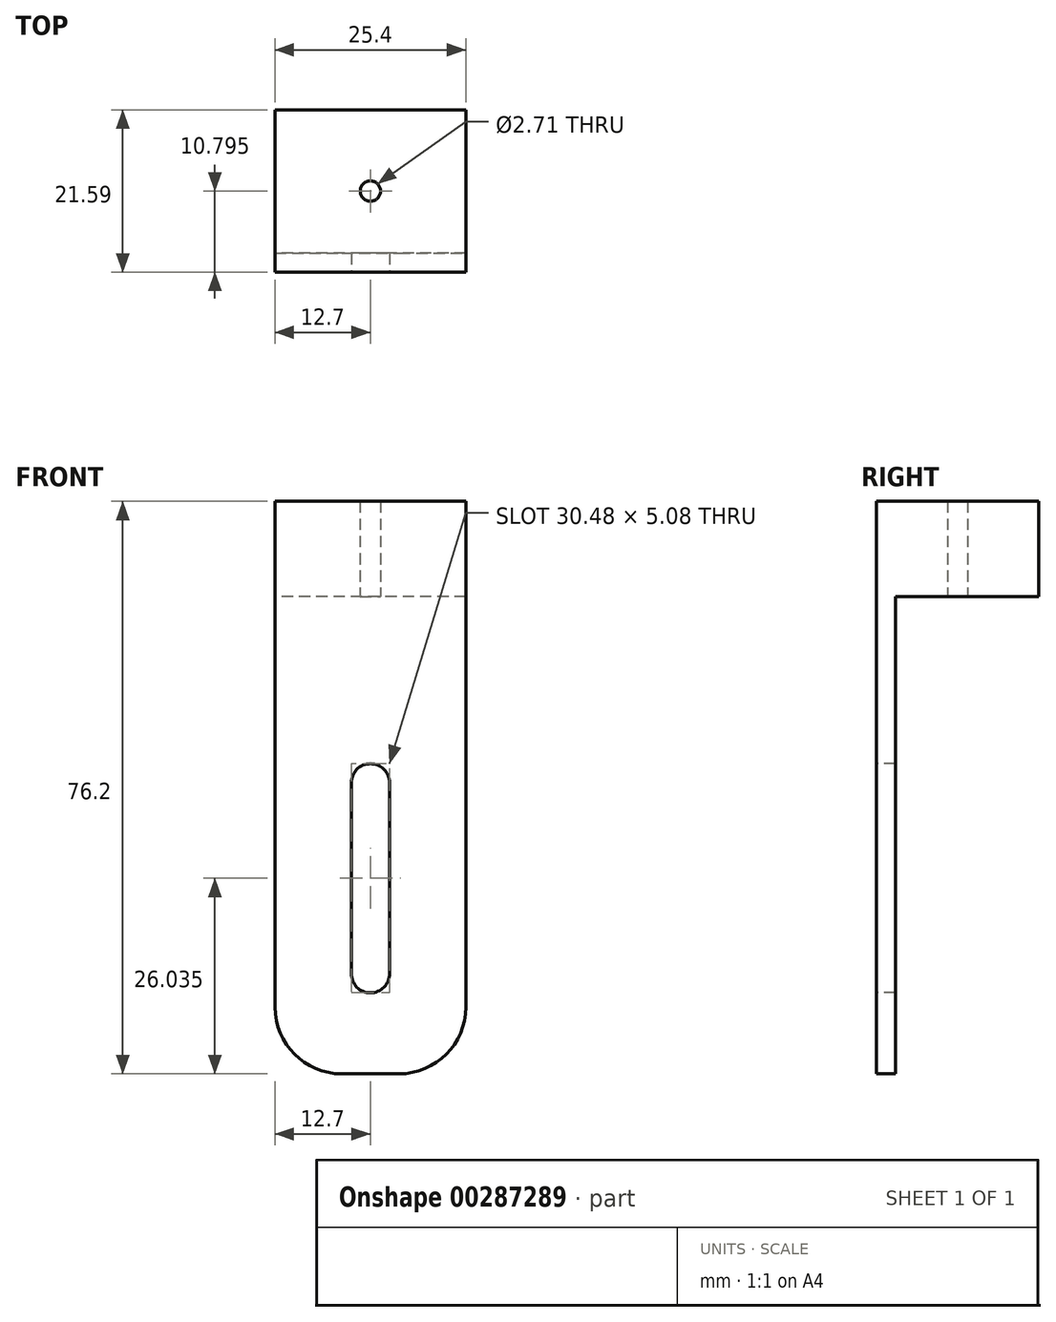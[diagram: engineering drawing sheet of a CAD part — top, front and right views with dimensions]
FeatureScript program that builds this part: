
annotation { "Feature Type Name" : "Feature", "Feature Type Description" : "" }
export const myFeature = defineFeature(function(context is Context, id is Id, definition is map)
    precondition{}
    {
        {
            var Q0;
            Q0=qCreatedBy(makeId("Front.planeOp"),FACE);
            var sketch = newSketch(context, id + "F0", { "sketchPlane" : qUnion([Q0])});
            skLineSegment(sketch, "E0.bottom", {"start": v(0, 0) * mm, "end": v(25.4, 0) * mm});
            skLineSegment(sketch, "E0.top", {"start": v(0, 76.2) * mm, "end": v(25.4, 76.2) * mm});
            skLineSegment(sketch, "E0.left", {"start": v(0, 0) * mm, "end": v(0, 76.2) * mm});
            skLineSegment(sketch, "E0.right", {"start": v(25.4, 0) * mm, "end": v(25.4, 76.2) * mm});
            skSolve(sketch);
        }
        {
            var Q0;
            Q0=qSketchRegion(id+"F0",true);
            extrude(context, id + "F1", {"entities" : qUnion([Q0]), "depth" : 2.54 * mm, "offsetDistance" : 25.4 * mm});
        }
        {
            var Q0;
            Q0=makeQuery(id+"F1.opExtrude","CAP_FACE",FACE,{"disambiguationData":[OSD([sQuery(id+"F0.wireOp",EDGE,"E0.bottom"),sQuery(id+"F0.wireOp",EDGE,"E0.top"),sQuery(id+"F0.wireOp",EDGE,"E0.left"),sQuery(id+"F0.wireOp",EDGE,"E0.right")])],"isStart":true});
            var sketch = newSketch(context, id + "F2", { "sketchPlane" : qUnion([Q0])});
            skLineSegment(sketch, "E1.bottom", {"start": v(-25.4, 76.2) * mm, "end": v(0, 76.2) * mm});
            skLineSegment(sketch, "E1.top", {"start": v(-25.4, 63.5) * mm, "end": v(0, 63.5) * mm});
            skLineSegment(sketch, "E1.left", {"start": v(-25.4, 76.2) * mm, "end": v(-25.4, 63.5) * mm});
            skLineSegment(sketch, "E1.right", {"start": v(0, 76.2) * mm, "end": v(0, 63.5) * mm});
            skSolve(sketch);
        }
        {
            var Q0;
            Q0=qSketchRegion(id+"F2",true);
            extrude(context, id + "F3", {"entities" : qUnion([Q0]), "operationType" : NewBodyOperationType.ADD, "depth" : 19.05 * mm, "offsetDistance" : 25.4 * mm});
        }
        {
            var Q0;
            Q0=makeQuery(id+"F3.opExtrude","SWEPT_FACE",FACE,{"disambiguationData":[OSD([sQuery(id+"F2.wireOp",EDGE,"E1.top")])]});
            var sketch = newSketch(context, id + "F4", { "sketchPlane" : qUnion([Q0])});
            skPoint(sketch, "E2", {"position": v(12.7, -8.26) * mm});
            skLineSegment(sketch, "E3", {"start": v(12.7, -19.05) * mm, "end": v(12.7, 0) * mm, "construction": true});
            skSolve(sketch);
        }
        {
            var Q0;
            Q0=sQuery(id+"F4.wireOp",VERTEX,"E2");
            var Q1;
            Q1=makeQuery(id+"F1.opExtrude","SWEPT_BODY",BODY,{"disambiguationData":[OSD([sQuery(id+"F0.wireOp",EDGE,"E0.bottom"),sQuery(id+"F0.wireOp",EDGE,"E0.top"),sQuery(id+"F0.wireOp",EDGE,"E0.left"),sQuery(id+"F0.wireOp",EDGE,"E0.right")])]});
            hole(context, id + "F5", {"style" : HoleStyle.SIMPLE, "endStyle" : HoleEndStyle.THROUGH, "standardTappedOrClearance" : lookupTablePath({ "standard" : "ANSI", "engagement" : "75%", "pitch" : "32 tpi", "size" : "#6", "type" : "Tapped" }), "standardBlindInLast" : lookupTablePath({ "standard" : "ANSI", "engagement" : "75%", "pitch" : "32 tpi", "size" : "#6", "type" : "Tapped" }), "holeDiameter" : 2.7 * mm, "majorDiameter" : 3.5 * mm, "showTappedDepth" : true, "isTappedThrough" : true, "tappedDepth" : 10.32 * mm, "tapClearance" : 3, "startFromSketch" : true, "locations" : qUnion([Q0]), "scope" : qUnion([Q1])});
        }
        {
            var Q0;
            Q0=makeQuery(id+"F1.opExtrude","CAP_FACE",FACE,{"disambiguationData":[OSD([sQuery(id+"F0.wireOp",EDGE,"E0.bottom"),sQuery(id+"F0.wireOp",EDGE,"E0.top"),sQuery(id+"F0.wireOp",EDGE,"E0.left"),sQuery(id+"F0.wireOp",EDGE,"E0.right")])],"isStart":false});
            var sketch = newSketch(context, id + "F6", { "sketchPlane" : qUnion([Q0])});
            skLineSegment(sketch, "E4", {"start": v(12.7, 38.74) * mm, "end": v(12.7, 13.34) * mm});
            skArc(sketch, "E5.0.startCap", {"start": v(10.16, 38.74) * mm, "mid": v(12.7, 41.28) * mm, "end": v(15.24, 38.74) * mm});
            skArc(sketch, "E5.0.endCap", {"start": v(15.24, 13.34) * mm, "mid": v(12.7, 10.8) * mm, "end": v(10.16, 13.34) * mm});
            skLineSegment(sketch, "E5.0.left", {"start": v(15.24, 38.74) * mm, "end": v(15.24, 13.33) * mm});
            skLineSegment(sketch, "E5.0.right", {"start": v(10.16, 38.74) * mm, "end": v(10.16, 13.34) * mm});
            skLineSegment(sketch, "E6", {"start": v(12.7, 0) * mm, "end": v(12.7, 76.2) * mm, "construction": true});
            skSolve(sketch);
        }
        {
            var Q0;
            Q0=qSketchRegion(id+"F6",true);
            extrude(context, id + "F7", {"entities" : qUnion([Q0]), "operationType" : NewBodyOperationType.REMOVE, "endBound" : BoundingType.THROUGH_ALL, "oppositeDirection" : true, "depth" : 25.4 * mm, "offsetDistance" : 25.4 * mm});
        }
        {
            var Q0;
            Q0=makeQuery(id+"F1.opExtrude","SWEPT_EDGE",EDGE,{"disambiguationData":[OSD([sQuery(id+"F0.wireOp",EDGE,"E0.bottom"),sQuery(id+"F0.wireOp",EDGE,"E0.left")])]});
            var Q1;
            Q1=makeQuery(id+"F1.opExtrude","SWEPT_EDGE",EDGE,{"disambiguationData":[OSD([sQuery(id+"F0.wireOp",EDGE,"E0.bottom"),sQuery(id+"F0.wireOp",EDGE,"E0.right")])]});
            fillet(context, id + "F8", {"entities" : qUnion([Q0, Q1]), "radius" : 8.9 * mm, "tangentPropagation" : true, "allowEdgeOverflow" : false});
        }
    });
